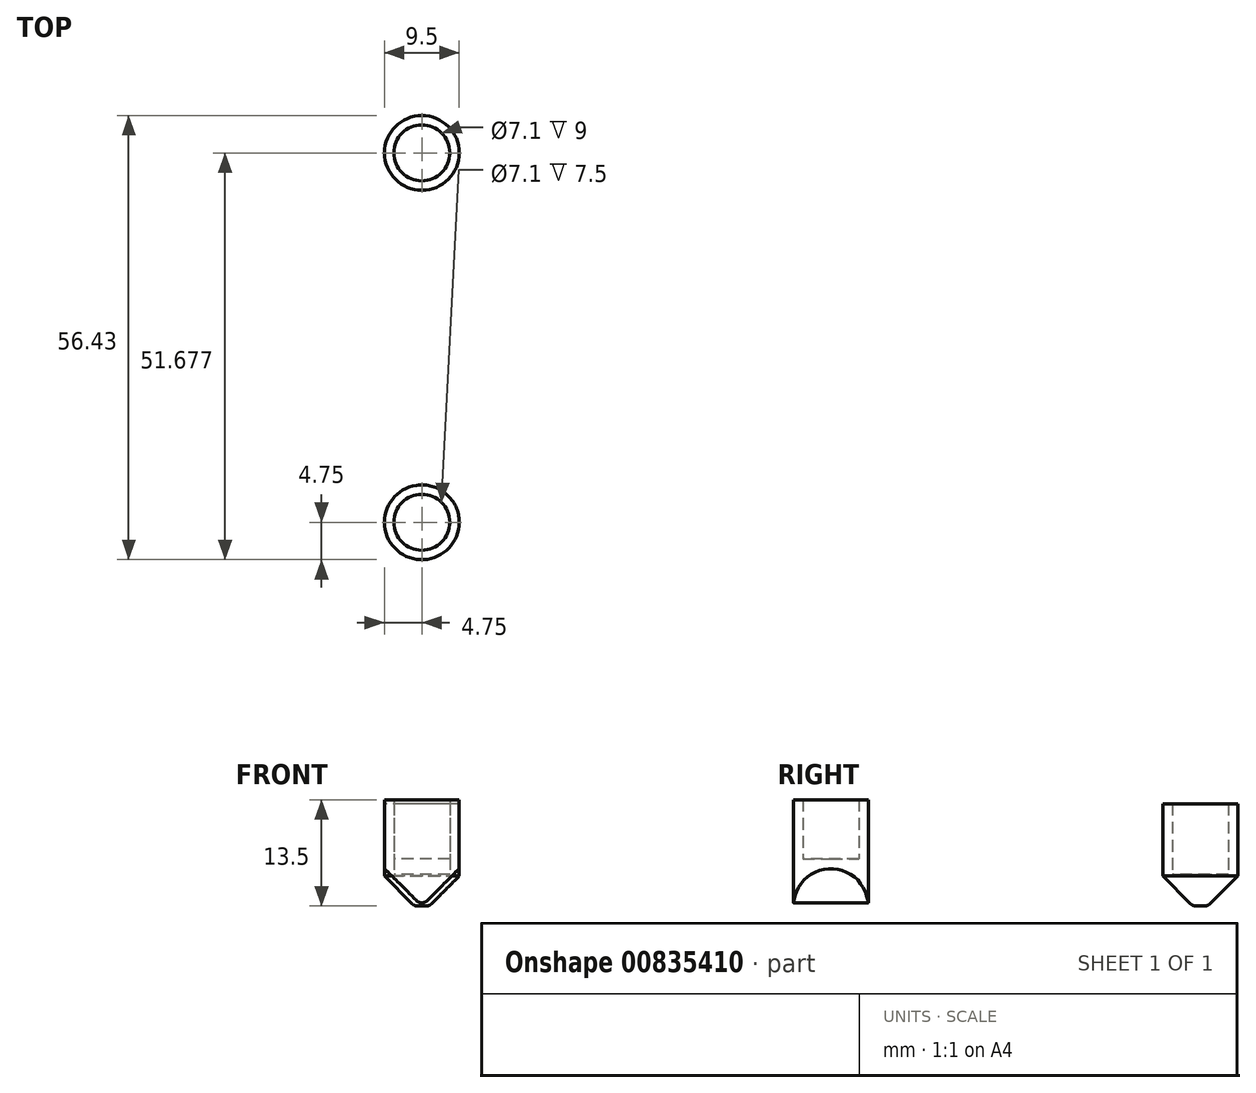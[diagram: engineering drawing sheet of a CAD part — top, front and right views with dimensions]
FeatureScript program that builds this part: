
annotation { "Feature Type Name" : "Feature", "Feature Type Description" : "" }
export const myFeature = defineFeature(function(context is Context, id is Id, definition is map)
    precondition{}
    {
        {
            var Q0;
            Q0=qCreatedBy(makeId("Top.planeOp"),FACE);
            var sketch = newSketch(context, id + "F0", { "sketchPlane" : qUnion([Q0])});
            skCircle(sketch, "E0", {"center": v(0, 0) * mm, "radius": 3.55 * mm});
            skCircle(sketch, "E1", {"center": v(0, 0) * mm, "radius": 4.75 * mm});
            skSolve(sketch);
        }
        {
            var Q0;
            Q0 = qSketchRegion(id + "F0", true);
            extrude(context, id + "F1", {"entities" : qUnion([Q0]), "depth" : 13.5 * mm, "offsetDistance" : 25 * mm});
        }
        {
            var Q0;
            Q0=makeQuery(id+"F0.imprint","IMPRINT",FACE,{"disambiguationData":[TD([[makeQuery(id+"F0.imprint","IMPRINT",EDGE,{"derivedFrom":sQuery(id+"F0.wireOp",EDGE,"E0")}),1.0]])]});
            extrude(context, id + "F2", {"entities" : qUnion([Q0]), "operationType" : NewBodyOperationType.ADD, "depth" : 6 * mm, "offsetDistance" : 25 * mm});
        }
        {
            var Q0;
            Q0=qCreatedBy(makeId("Front.planeOp"),FACE);
            var sketch = newSketch(context, id + "F3", { "sketchPlane" : qUnion([Q0])});
            skLineSegment(sketch, "E2", {"start": v(0, 0) * mm, "end": v(-5.82, 5.82) * mm});
            skLineSegment(sketch, "E3", {"start": v(-5.82, 5.82) * mm, "end": v(-5.82, -4.8) * mm});
            skLineSegment(sketch, "E4", {"start": v(-5.82, -4.8) * mm, "end": v(6.57, -4.8) * mm});
            skLineSegment(sketch, "E5", {"start": v(6.57, -4.8) * mm, "end": v(6.57, 6.57) * mm});
            skLineSegment(sketch, "E6", {"start": v(6.57, 6.57) * mm, "end": v(0, 0) * mm});
            skSolve(sketch);
        }
        {
            var Q0;
            Q0 = qSketchRegion(id + "F3", true);
            extrude(context, id + "F4", {"entities" : qUnion([Q0]), "operationType" : NewBodyOperationType.REMOVE, "endBound" : BoundingType.SYMMETRIC, "depth" : 25 * mm, "offsetDistance" : 25 * mm});
        }
        {
            var Q0;
            Q0=makeQuery(id+"F4.boolean.opBoolean","COPY",EDGE,{"derivedFrom":makeQuery(id+"F4.opExtrude","SWEPT_EDGE",EDGE,{"disambiguationData":[OSD([sQuery(id+"F3.wireOp",EDGE,"E2"),sQuery(id+"F3.wireOp",EDGE,"E6")])]})});
            fillet(context, id + "F5", {"entities" : qUnion([Q0]), "radius" : 1 * mm, "tangentPropagation" : true, "allowEdgeOverflow" : false});
        }
        {
            var Q0;
            Q0=qCreatedBy(makeId("Top.planeOp"),FACE);
            var sketch = newSketch(context, id + "F6", { "sketchPlane" : qUnion([Q0])});
            skCircle(sketch, "E7", {"center": v(0, 46.93) * mm, "radius": 3.55 * mm});
            skCircle(sketch, "E8", {"center": v(0, 46.93) * mm, "radius": 4.75 * mm});
            skSolve(sketch);
        }
        {
            var Q0;
            Q0 = qSketchRegion(id + "F6", true);
            extrude(context, id + "F7", {"entities" : qUnion([Q0]), "depth" : 13 * mm, "offsetDistance" : 25 * mm});
        }
        {
            var Q0;
            Q0=makeQuery(id+"F6.imprint","IMPRINT",FACE,{"disambiguationData":[TD([[makeQuery(id+"F6.imprint","IMPRINT",EDGE,{"derivedFrom":sQuery(id+"F6.wireOp",EDGE,"E7")}),1.0]])]});
            extrude(context, id + "F8", {"entities" : qUnion([Q0]), "operationType" : NewBodyOperationType.ADD, "depth" : 4 * mm, "offsetDistance" : 25 * mm});
        }
        {
            var Q0;
            Q0=makeQuery(id+"F7.opExtrude","CAP_EDGE",EDGE,{"disambiguationData":[OSD([sQuery(id+"F6.wireOp",EDGE,"E8")])],"isStart":true});
            chamfer(context, id + "F9", {"entities" : qUnion([Q0]), "width" : 3.8 * mm, "tangentPropagation" : true});
        }
        {
            var Q0;
            {var subQ0=sQuery(id+"F6.wireOp",EDGE,"E7");var subQ1=sQuery(id+"F6.wireOp",EDGE,"E8");Q0=makeQuery(id+"F9.opChamfer","BLEND_EDGE",EDGE,{"blendedFrom":[makeQuery(id+"F7.opExtrude","CAP_EDGE",EDGE,{"disambiguationData":[OSD([subQ1])],"isStart":true}),makeQuery(id+"F8.boolean.opBoolean","MERGE",FACE,{"derivedFrom":[makeQuery(id+"F7.opExtrude","CAP_FACE",FACE,{"disambiguationData":[OSD([subQ0,subQ1])],"isStart":true}),makeQuery(id+"F8.opExtrude","CAP_FACE",FACE,{"disambiguationData":[OSD([subQ0])],"isStart":true})]})],"blendedInto":[makeQuery(id+"F8.boolean.opBoolean","MERGE",FACE,{"derivedFrom":[makeQuery(id+"F7.opExtrude","CAP_FACE",FACE,{"disambiguationData":[OSD([subQ0,subQ1])],"isStart":true}),makeQuery(id+"F8.opExtrude","CAP_FACE",FACE,{"disambiguationData":[OSD([subQ0])],"isStart":true})]})]});}
            fillet(context, id + "F10", {"entities" : qUnion([Q0]), "radius" : 1 * mm, "tangentPropagation" : true, "allowEdgeOverflow" : false});
        }
    });
